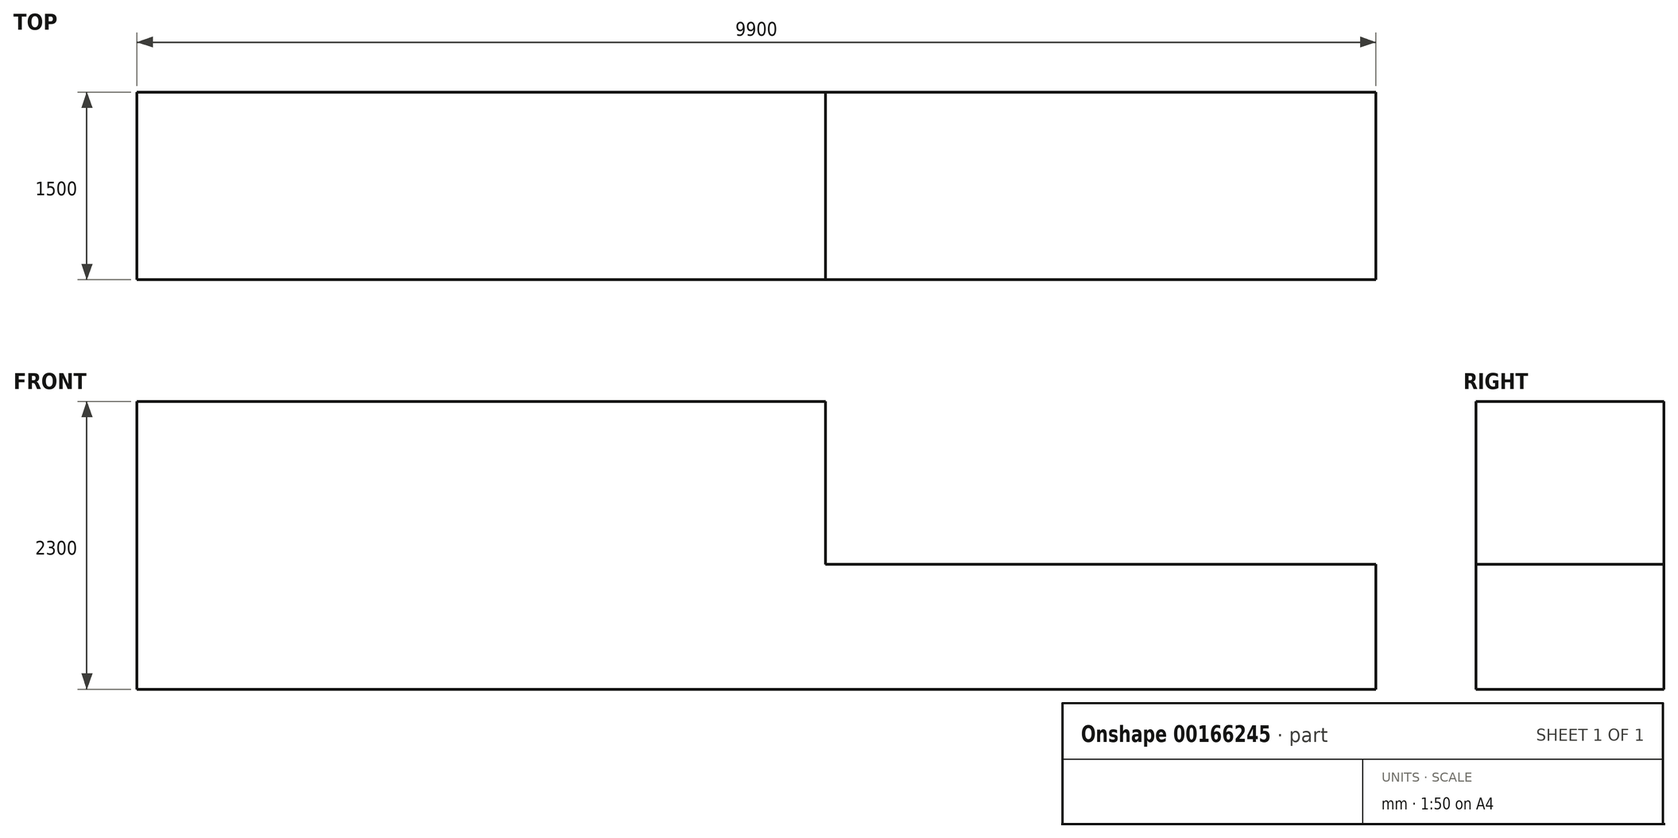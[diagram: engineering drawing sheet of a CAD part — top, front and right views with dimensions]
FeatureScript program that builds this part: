
annotation { "Feature Type Name" : "Feature", "Feature Type Description" : "" }
export const myFeature = defineFeature(function(context is Context, id is Id, definition is map)
    precondition{}
    {
        {
            var Q0;
            Q0=qCreatedBy(makeId("Top.planeOp"),FACE);
            var sketch = newSketch(context, id + "F0", { "sketchPlane" : qUnion([Q0])});
            skLineSegment(sketch, "E0.bottom", {"start": v(4950, 750) * mm, "end": v(-4950, 750) * mm});
            skLineSegment(sketch, "E0.top", {"start": v(4950, -750) * mm, "end": v(-4950, -750) * mm});
            skLineSegment(sketch, "E0.left", {"start": v(4950, 750) * mm, "end": v(4950, -750) * mm});
            skLineSegment(sketch, "E0.right", {"start": v(-4950, 750) * mm, "end": v(-4950, -750) * mm});
            skPoint(sketch, "E0.middle", {"position": v(0, 0) * mm});
            skSolve(sketch);
        }
        {
            var Q0;
            Q0 = qSketchRegion(id + "F0", true);
            extrude(context, id + "F2", {"entities" : qUnion([Q0]), "depth" : 1000 * mm});
        }
        {
            var Q0;
            Q0=makeQuery(id+"F2.opExtrude","CAP_FACE",FACE,{"disambiguationData":[OSD([sQuery(id+"F0.wireOp",EDGE,"E0.bottom"),sQuery(id+"F0.wireOp",EDGE,"E0.top"),sQuery(id+"F0.wireOp",EDGE,"E0.left"),sQuery(id+"F0.wireOp",EDGE,"E0.right")])],"isStart":false});
            var sketch = newSketch(context, id + "F1", { "sketchPlane" : qUnion([Q0])});
            skLineSegment(sketch, "E1.bottom", {"start": v(-4950, -750) * mm, "end": v(550, -750) * mm});
            skLineSegment(sketch, "E1.top", {"start": v(-4950, 750) * mm, "end": v(550, 750) * mm});
            skLineSegment(sketch, "E1.left", {"start": v(-4950, -750) * mm, "end": v(-4950, 750) * mm});
            skLineSegment(sketch, "E1.right", {"start": v(550, -750) * mm, "end": v(550, 750) * mm});
            skSolve(sketch);
        }
        {
            var Q0;
            Q0=makeQuery(id+"F1.imprint","IMPRINT",FACE,{"disambiguationData":[TD([[makeQuery(id+"F1.imprint","IMPRINT",EDGE,{"derivedFrom":sQuery(id+"F1.wireOp",EDGE,"E1.bottom")}),-1.0]])]});
            extrude(context, id + "F3", {"entities" : qUnion([Q0]), "operationType" : NewBodyOperationType.ADD, "depth" : 1300 * mm});
        }
    });
